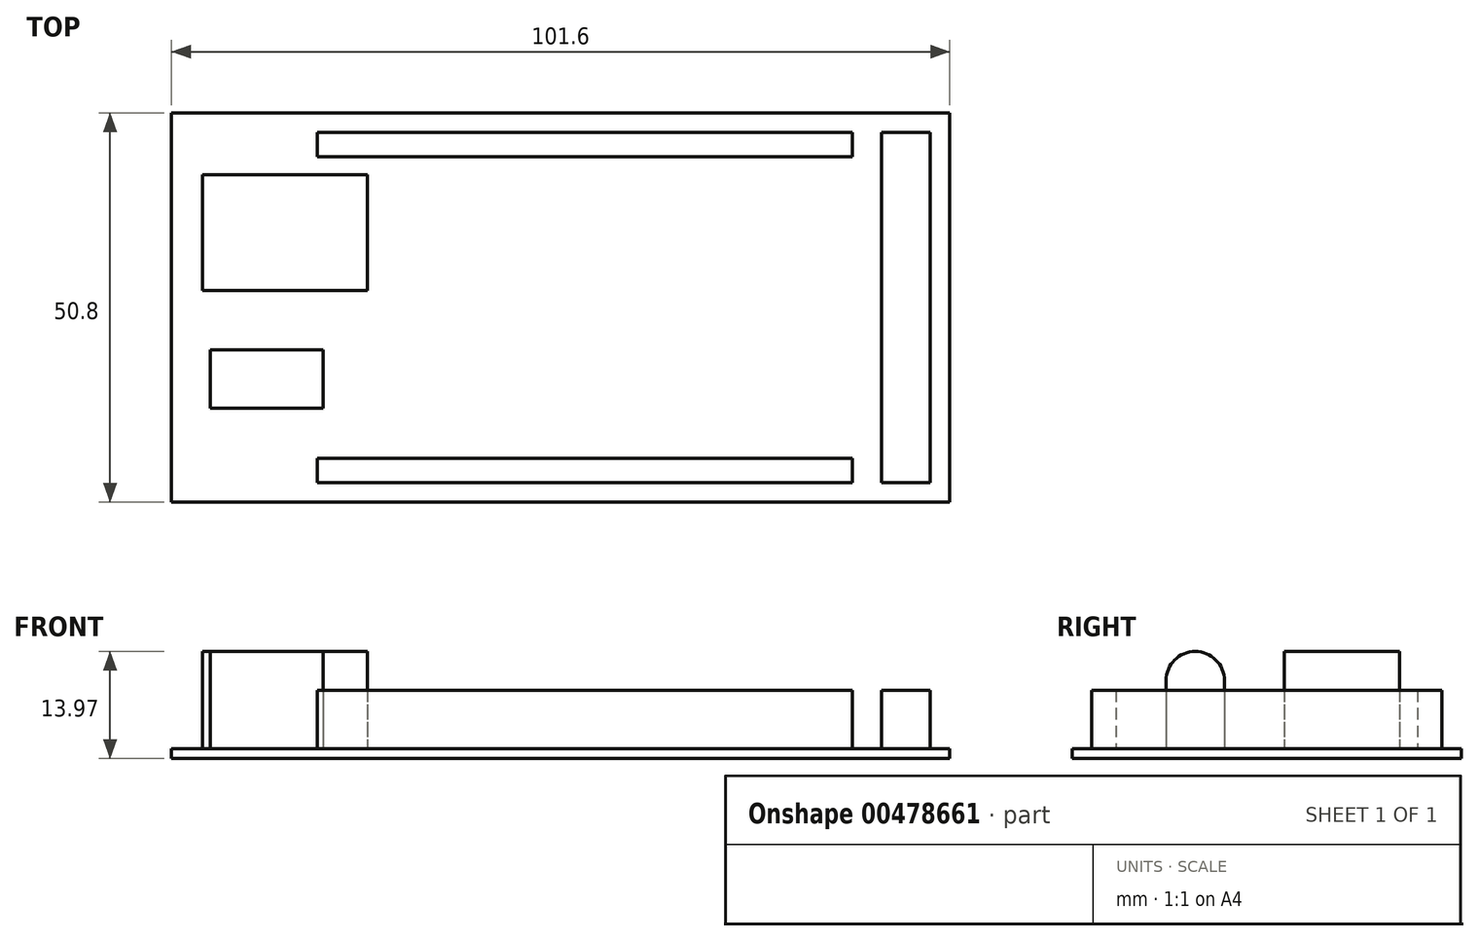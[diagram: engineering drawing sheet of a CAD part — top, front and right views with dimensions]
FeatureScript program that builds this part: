
annotation { "Feature Type Name" : "Feature", "Feature Type Description" : "" }
export const myFeature = defineFeature(function(context is Context, id is Id, definition is map)
    precondition{}
    {
        {
            var Q0;
            Q0=qCreatedBy(makeId("Top.planeOp"),FACE);
            var sketch = newSketch(context, id + "F0", { "sketchPlane" : qUnion([Q0])});
            skLineSegment(sketch, "E0.bottom", {"start": v(50.8, 25.4) * mm, "end": v(-50.8, 25.4) * mm});
            skLineSegment(sketch, "E0.top", {"start": v(50.8, -25.4) * mm, "end": v(-50.8, -25.4) * mm});
            skLineSegment(sketch, "E0.left", {"start": v(50.8, 25.4) * mm, "end": v(50.8, -25.4) * mm});
            skLineSegment(sketch, "E0.right", {"start": v(-50.8, 25.4) * mm, "end": v(-50.8, -25.4) * mm});
            skPoint(sketch, "E0.middle", {"position": v(0, 0) * mm});
            skSolve(sketch);
        }
        {
            var Q0;
            Q0=makeQuery(id+"F0.imprint","IMPRINT",FACE,{"disambiguationData":[TD([[makeQuery(id+"F0.imprint","IMPRINT",EDGE,{"derivedFrom":sQuery(id+"F0.wireOp",EDGE,"E0.bottom")}),1.0]])]});
            extrude(context, id + "F1", {"entities" : qUnion([Q0]), "depth" : 1.27 * mm});
        }
        {
            var Q0;
            Q0=makeQuery(id+"F1.opExtrude","CAP_FACE",FACE,{"disambiguationData":[OSD([sQuery(id+"F0.wireOp",EDGE,"E0.bottom"),sQuery(id+"F0.wireOp",EDGE,"E0.top"),sQuery(id+"F0.wireOp",EDGE,"E0.left"),sQuery(id+"F0.wireOp",EDGE,"E0.right")])],"isStart":false});
            var sketch = newSketch(context, id + "F2", { "sketchPlane" : qUnion([Q0])});
            skLineSegment(sketch, "E1.bottom", {"start": v(-31.75, 22.86) * mm, "end": v(38.1, 22.86) * mm});
            skLineSegment(sketch, "E1.top", {"start": v(-31.75, 19.68) * mm, "end": v(38.1, 19.68) * mm});
            skLineSegment(sketch, "E1.left", {"start": v(-31.75, 22.86) * mm, "end": v(-31.75, 19.68) * mm});
            skLineSegment(sketch, "E1.right", {"start": v(38.1, 22.86) * mm, "end": v(38.1, 19.69) * mm});
            skLineSegment(sketch, "E2.bottom", {"start": v(41.91, 22.86) * mm, "end": v(48.26, 22.86) * mm});
            skLineSegment(sketch, "E2.top", {"start": v(41.91, -22.86) * mm, "end": v(48.26, -22.86) * mm});
            skLineSegment(sketch, "E2.left", {"start": v(41.91, 22.86) * mm, "end": v(41.91, -22.86) * mm});
            skLineSegment(sketch, "E2.right", {"start": v(48.26, 22.86) * mm, "end": v(48.26, -22.86) * mm});
            skLineSegment(sketch, "E3.bottom", {"start": v(38.1, -19.69) * mm, "end": v(-31.75, -19.69) * mm});
            skLineSegment(sketch, "E3.top", {"start": v(38.1, -22.86) * mm, "end": v(-31.75, -22.86) * mm});
            skLineSegment(sketch, "E3.left", {"start": v(38.1, -19.69) * mm, "end": v(38.1, -22.86) * mm});
            skLineSegment(sketch, "E3.right", {"start": v(-31.75, -19.69) * mm, "end": v(-31.75, -22.86) * mm});
            skSolve(sketch);
        }
        {
            var Q0;
            Q0=qSketchRegion(id+"F2",true);
            extrude(context, id + "F3", {"entities" : qUnion([Q0]), "operationType" : NewBodyOperationType.ADD, "depth" : 7.62 * mm});
        }
        {
            var Q0;
            Q0=makeQuery(id+"F1.opExtrude","CAP_FACE",FACE,{"disambiguationData":[OSD([sQuery(id+"F0.wireOp",EDGE,"E0.bottom"),sQuery(id+"F0.wireOp",EDGE,"E0.top"),sQuery(id+"F0.wireOp",EDGE,"E0.left"),sQuery(id+"F0.wireOp",EDGE,"E0.right")])],"isStart":false});
            var sketch = newSketch(context, id + "F4", { "sketchPlane" : qUnion([Q0])});
            skLineSegment(sketch, "E4.bottom", {"start": v(-46.75, 17.3) * mm, "end": v(-25.22, 17.3) * mm});
            skLineSegment(sketch, "E4.top", {"start": v(-46.75, 2.25) * mm, "end": v(-25.22, 2.25) * mm});
            skLineSegment(sketch, "E4.left", {"start": v(-46.75, 17.3) * mm, "end": v(-46.75, 2.25) * mm});
            skLineSegment(sketch, "E4.right", {"start": v(-25.22, 17.3) * mm, "end": v(-25.22, 2.25) * mm});
            skLineSegment(sketch, "E5.bottom", {"start": v(-45.73, -5.55) * mm, "end": v(-30.97, -5.55) * mm});
            skLineSegment(sketch, "E5.top", {"start": v(-45.73, -13.17) * mm, "end": v(-30.97, -13.17) * mm});
            skLineSegment(sketch, "E5.left", {"start": v(-45.73, -5.55) * mm, "end": v(-45.73, -13.17) * mm});
            skLineSegment(sketch, "E5.right", {"start": v(-30.97, -5.55) * mm, "end": v(-30.97, -13.17) * mm});
            skSolve(sketch);
        }
        {
            var Q0;
            Q0=qSketchRegion(id+"F4",true);
            extrude(context, id + "F5", {"entities" : qUnion([Q0]), "operationType" : NewBodyOperationType.ADD, "depth" : 12.7 * mm});
        }
        {
            var Q0;
            Q0=makeQuery(id+"F5.opExtrude","CAP_EDGE",EDGE,{"disambiguationData":[OSD([sQuery(id+"F4.wireOp",EDGE,"E5.top")])],"isStart":false});
            var Q1;
            Q1=makeQuery(id+"F5.opExtrude","CAP_EDGE",EDGE,{"disambiguationData":[OSD([sQuery(id+"F4.wireOp",EDGE,"E5.bottom")])],"isStart":false});
            fillet(context, id + "F6", {"entities" : qUnion([Q0, Q1]), "radius" : 3.8 * mm, "tangentPropagation" : true, "allowEdgeOverflow" : false});
        }
    });
